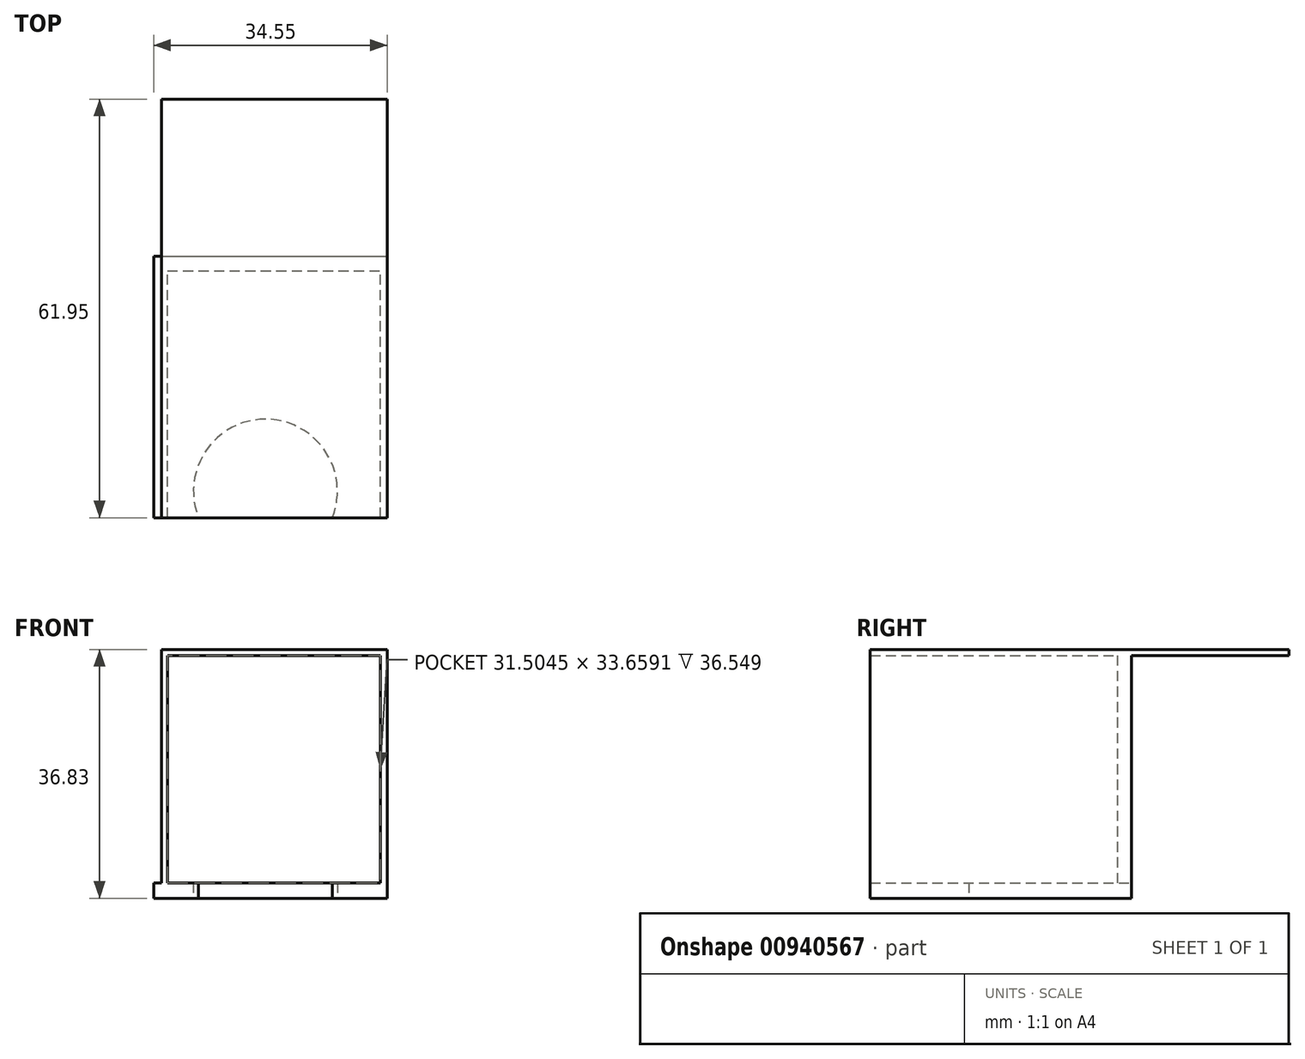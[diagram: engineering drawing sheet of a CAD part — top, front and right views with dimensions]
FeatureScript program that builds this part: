
annotation { "Feature Type Name" : "Feature", "Feature Type Description" : "" }
export const myFeature = defineFeature(function(context is Context, id is Id, definition is map)
    precondition{}
    {
        {
            var Q0;
            Q0=qCreatedBy(makeId("Top.planeOp"),FACE);
            var sketch = newSketch(context, id + "F0", { "sketchPlane" : qUnion([Q0])});
            skLineSegment(sketch, "E0.bottom", {"start": v(-56.35, 25.98) * mm, "end": v(-55.16, 25.98) * mm});
            skLineSegment(sketch, "E0.top", {"start": v(-56.35, -12.7) * mm, "end": v(-55.16, -12.7) * mm});
            skLineSegment(sketch, "E0.left", {"start": v(-56.35, 25.98) * mm, "end": v(-56.35, -12.7) * mm});
            skLineSegment(sketch, "E0.right", {"start": v(-55.16, 25.98) * mm, "end": v(-55.16, -12.7) * mm});
            skLineSegment(sketch, "E1.bottom", {"start": v(-55.16, 25.98) * mm, "end": v(-21.8, 25.98) * mm});
            skLineSegment(sketch, "E1.top", {"start": v(-55.16, 23.86) * mm, "end": v(-21.8, 23.86) * mm});
            skLineSegment(sketch, "E1.left", {"start": v(-55.16, 25.98) * mm, "end": v(-55.16, 23.86) * mm});
            skLineSegment(sketch, "E1.right", {"start": v(-21.8, 25.98) * mm, "end": v(-21.8, 23.86) * mm});
            skLineSegment(sketch, "E2.bottom", {"start": v(-21.8, 23.86) * mm, "end": v(-23.8, 23.86) * mm});
            skLineSegment(sketch, "E2.top", {"start": v(-21.8, -12.7) * mm, "end": v(-23.8, -12.7) * mm});
            skLineSegment(sketch, "E2.left", {"start": v(-21.8, 23.86) * mm, "end": v(-21.8, -12.7) * mm});
            skLineSegment(sketch, "E2.right", {"start": v(-23.8, 23.86) * mm, "end": v(-23.8, -12.7) * mm});
            skLineSegment(sketch, "E3", {"start": v(-55.16, -12.7) * mm, "end": v(-23.8, -12.7) * mm});
            skArc(sketch, "E4", {"start": v(-29.9, -12.7) * mm, "mid": v(-39.8, 1.89) * mm, "end": v(-49.7, -12.7) * mm});
            skSolve(sketch);
        }
        {
            var Q0;
            {var subQ3=sQuery(id+"F0.wireOp",EDGE,"E0.bottom");Q0=makeQuery(id+"F0.imprint","IMPRINT",FACE,{"disambiguationData":[TD([[makeQuery(id+"F0.imprint","IMPRINT",EDGE,{"derivedFrom":subQ3}),-1.0]])]});}
            var Q1;
            Q1=makeQuery(id+"F0.imprint","IMPRINT",FACE,{"disambiguationData":[TD([[makeQuery(id+"F0.imprint","IMPRINT",EDGE,{"derivedFrom":sQuery(id+"F0.wireOp",EDGE,"E2.top")}),-1.0]])]});
            var Q2;
            {var subQ5=sQuery(id+"F0.wireOp",EDGE,"E1.bottom");Q2=makeQuery(id+"F0.imprint","IMPRINT",FACE,{"disambiguationData":[TD([[makeQuery(id+"F0.imprint","IMPRINT",EDGE,{"derivedFrom":subQ5}),-1.0]])]});}
            var Q3;
            {var subQ0=sQuery(id+"F0.wireOp",EDGE,"E2.right");Q3=makeQuery(id+"F0.imprint","IMPRINT",FACE,{"disambiguationData":[TD([[makeQuery(id+"F0.imprint","IMPRINT",EDGE,{"derivedFrom":subQ0}),-1.0]])]});}
            extrude(context, id + "F1", {"entities" : qUnion([Q0, Q1, Q2, Q3]), "depth" : 2.3 * mm, "offsetDistance" : 25.4 * mm});
        }
        {
            var Q0;
            {var subQ5=sQuery(id+"F0.wireOp",EDGE,"E1.bottom");Q0=makeQuery(id+"F0.imprint","IMPRINT",FACE,{"disambiguationData":[TD([[makeQuery(id+"F0.imprint","IMPRINT",EDGE,{"derivedFrom":subQ5}),-1.0]])]});}
            extrude(context, id + "F2", {"entities" : qUnion([Q0]), "operationType" : NewBodyOperationType.ADD, "depth" : 36.83 * mm, "offsetDistance" : 25.4 * mm});
        }
        {
            var Q0;
            Q0=makeQuery(id+"F2.opExtrude","SWEPT_FACE",FACE,{"disambiguationData":[OSD([sQuery(id+"F0.wireOp",EDGE,"E1.top")])]});
            var sketch = newSketch(context, id + "F3", { "sketchPlane" : qUnion([Q0])});
            skLineSegment(sketch, "E5", {"start": v(-55.16, 35.95) * mm, "end": v(-21.8, 35.95) * mm});
            skSolve(sketch);
        }
        {
            var Q0;
            Q0 = qSketchRegion(id + "F3", true);
            var Q1;
            {var subQ0=sQuery(id+"F3.wireOp",EDGE,"E5");Q1=makeQuery(id+"F3.imprint","IMPRINT",FACE,{"disambiguationData":[TD([[makeQuery(id+"F3.imprint","IMPRINT",EDGE,{"derivedFrom":subQ0}),1.0]])]});}
            extrude(context, id + "F4", {"entities" : qUnion([Q0, Q1]), "operationType" : NewBodyOperationType.ADD, "depth" : 36.55 * mm, "offsetDistance" : 25.4 * mm, "hasSecondDirection" : true, "secondDirectionOppositeDirection" : true, "secondDirectionDepth" : 25.4 * mm});
        }
        {
            var Q0;
            Q0=makeQuery(id+"F2.opExtrude","SWEPT_FACE",FACE,{"disambiguationData":[OSD([sQuery(id+"F0.wireOp",EDGE,"E1.top")])]});
            var sketch = newSketch(context, id + "F5", { "sketchPlane" : qUnion([Q0])});
            skLineSegment(sketch, "E6", {"start": v(-54.3, 2.29) * mm, "end": v(-54.3, 35.95) * mm});
            skSolve(sketch);
        }
        {
            var Q0;
            Q0 = qSketchRegion(id + "F5", true);
            var Q1;
            {var subQ0=sQuery(id+"F5.wireOp",EDGE,"E6");Q1=makeQuery(id+"F5.imprint","IMPRINT",FACE,{"disambiguationData":[TD([[makeQuery(id+"F5.imprint","IMPRINT",EDGE,{"derivedFrom":subQ0}),1.0]])]});}
            extrude(context, id + "F6", {"entities" : qUnion([Q0, Q1]), "operationType" : NewBodyOperationType.ADD, "depth" : 36.55 * mm, "offsetDistance" : 25.4 * mm});
        }
        {
            var Q0;
            Q0=makeQuery(id+"F2.opExtrude","SWEPT_FACE",FACE,{"disambiguationData":[OSD([sQuery(id+"F0.wireOp",EDGE,"E1.top")])]});
            var sketch = newSketch(context, id + "F7", { "sketchPlane" : qUnion([Q0])});
            skLineSegment(sketch, "E7", {"start": v(-22.8, 35.95) * mm, "end": v(-22.8, 2.29) * mm});
            skSolve(sketch);
        }
        {
            var Q0;
            Q0 = qSketchRegion(id + "F7", true);
            var Q1;
            {var subQ0=sQuery(id+"F7.wireOp",EDGE,"E7");Q1=makeQuery(id+"F7.imprint","IMPRINT",FACE,{"disambiguationData":[TD([[makeQuery(id+"F7.imprint","IMPRINT",EDGE,{"derivedFrom":subQ0}),1.0]])]});}
            extrude(context, id + "F8", {"entities" : qUnion([Q0, Q1]), "operationType" : NewBodyOperationType.ADD, "depth" : 36.55 * mm, "offsetDistance" : 25.4 * mm});
        }
    });
